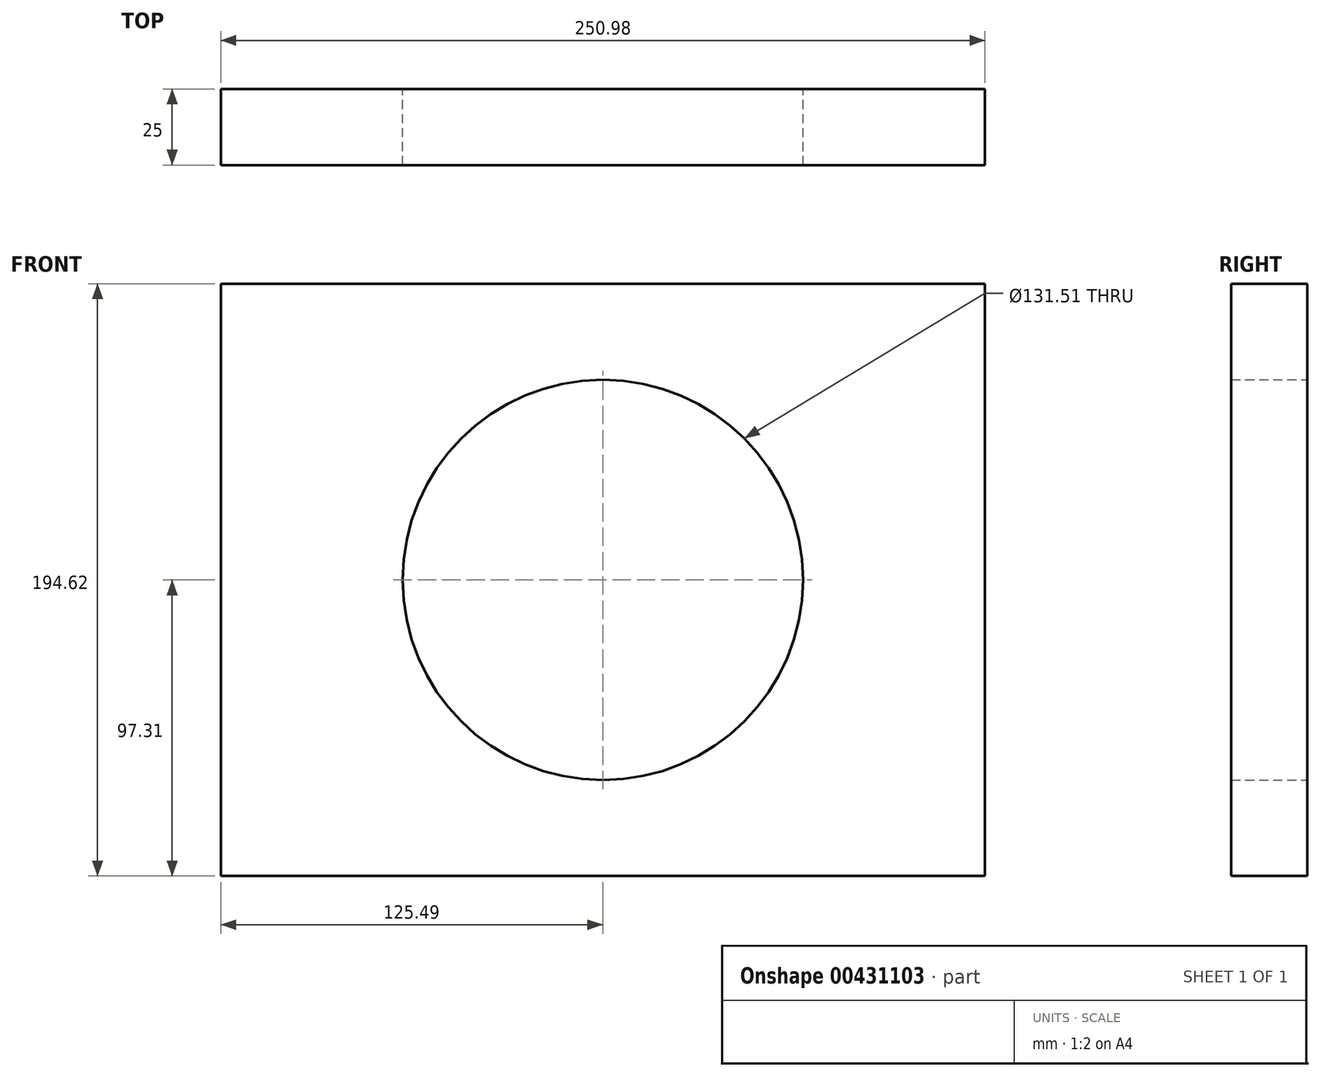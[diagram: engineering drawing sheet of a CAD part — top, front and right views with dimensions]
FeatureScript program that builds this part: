
annotation { "Feature Type Name" : "Feature", "Feature Type Description" : "" }
export const myFeature = defineFeature(function(context is Context, id is Id, definition is map)
    precondition{}
    {
        {
            var Q0;
            Q0=qCreatedBy(makeId("Front.planeOp"),FACE);
            var sketch = newSketch(context, id + "F0", { "sketchPlane" : qUnion([Q0])});
            skLineSegment(sketch, "E0.bottom", {"start": v(125.5, 97.31) * mm, "end": v(-125.5, 97.31) * mm});
            skLineSegment(sketch, "E0.top", {"start": v(125.5, -97.31) * mm, "end": v(-125.5, -97.31) * mm});
            skLineSegment(sketch, "E0.left", {"start": v(125.5, 97.31) * mm, "end": v(125.5, -97.31) * mm});
            skLineSegment(sketch, "E0.right", {"start": v(-125.5, 97.31) * mm, "end": v(-125.5, -97.31) * mm});
            skPoint(sketch, "E0.middle", {"position": v(0, 0) * mm});
            skCircle(sketch, "E1", {"center": v(0, 0) * mm, "radius": 65.75 * mm});
            skSolve(sketch);
        }
        {
            var Q0;
            Q0 = qSketchRegion(id + "F0", true);
            extrude(context, id + "F1", {"entities" : qUnion([Q0]), "depth" : 25 * mm});
        }
        {
            var Q0;
            Q0=makeQuery(id+"F1.opExtrude","CAP_FACE",FACE,{"disambiguationData":[OSD([sQuery(id+"F0.wireOp",EDGE,"E0.bottom"),sQuery(id+"F0.wireOp",EDGE,"E0.top"),sQuery(id+"F0.wireOp",EDGE,"E0.left"),sQuery(id+"F0.wireOp",EDGE,"E0.right"),sQuery(id+"F0.wireOp",EDGE,"E1")])],"isStart":true});
            extrude(context, id + "F2", {"entities" : qUnion([Q0]), "operationType" : NewBodyOperationType.ADD, "oppositeDirection" : true, "depth" : 25 * mm});
        }
    });
